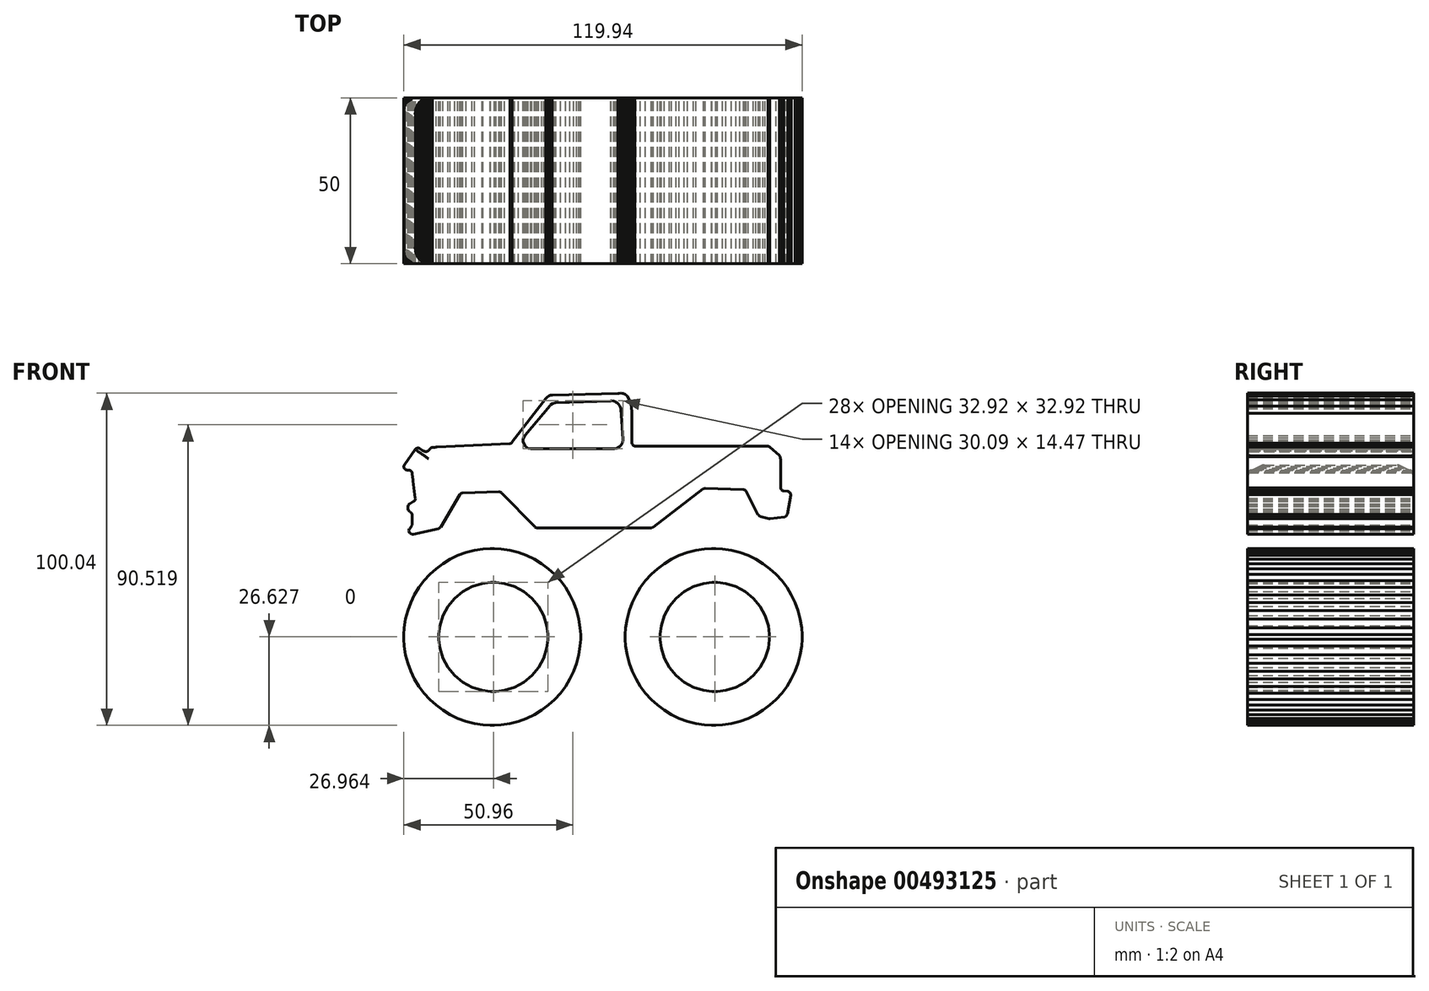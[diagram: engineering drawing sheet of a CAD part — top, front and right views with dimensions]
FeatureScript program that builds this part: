
annotation { "Feature Type Name" : "Feature", "Feature Type Description" : "" }
export const myFeature = defineFeature(function(context is Context, id is Id, definition is map)
    precondition{}
    {
        {
            var Q0;
            Q0=qCreatedBy(makeId("Front.planeOp"),FACE);
            var sketch = newSketch(context, id + "F0", { "sketchPlane" : qUnion([Q0])});
            skLineSegment(sketch, "E0", {"start": v(5.26, 34.16) * mm, "end": v(5.06, 33.96) * mm});
            skLineSegment(sketch, "E1", {"start": v(5.06, 33.96) * mm, "end": v(4.94, 33.85) * mm});
            skLineSegment(sketch, "E2", {"start": v(4.94, 33.85) * mm, "end": v(4.26, 33.45) * mm});
            skLineSegment(sketch, "E3", {"start": v(4.26, 33.45) * mm, "end": v(3.56, 33.27) * mm});
            skLineSegment(sketch, "E4", {"start": v(3.56, 33.27) * mm, "end": v(3.33, 33.27) * mm});
            skLineSegment(sketch, "E5", {"start": v(3.33, 33.27) * mm, "end": v(-21.56, 33.27) * mm});
            skLineSegment(sketch, "E6", {"start": v(-21.56, 33.27) * mm, "end": v(-21.8, 33.27) * mm});
            skLineSegment(sketch, "E7", {"start": v(-21.8, 33.27) * mm, "end": v(-22.53, 33.46) * mm});
            skLineSegment(sketch, "E8", {"start": v(-22.53, 33.46) * mm, "end": v(-23.33, 34) * mm});
            skLineSegment(sketch, "E9", {"start": v(-23.33, 34) * mm, "end": v(-23.86, 34.79) * mm});
            skLineSegment(sketch, "E10", {"start": v(-23.86, 34.79) * mm, "end": v(-24.05, 35.51) * mm});
            skLineSegment(sketch, "E11", {"start": v(-24.05, 35.51) * mm, "end": v(-24.05, 35.76) * mm});
            skLineSegment(sketch, "E12", {"start": v(-24.05, 35.76) * mm, "end": v(-24.05, 35.97) * mm});
            skLineSegment(sketch, "E13", {"start": v(-24.05, 35.97) * mm, "end": v(-23.9, 36.61) * mm});
            skLineSegment(sketch, "E14", {"start": v(-23.9, 36.61) * mm, "end": v(-23.56, 37.25) * mm});
            skLineSegment(sketch, "E15", {"start": v(-23.56, 37.25) * mm, "end": v(-23.47, 37.36) * mm});
            skLineSegment(sketch, "E16", {"start": v(-23.47, 37.36) * mm, "end": v(-15.9, 46.32) * mm});
            skLineSegment(sketch, "E17", {"start": v(-15.9, 46.32) * mm, "end": v(-15.8, 46.46) * mm});
            skLineSegment(sketch, "E18", {"start": v(-15.8, 46.46) * mm, "end": v(-15.11, 46.95) * mm});
            skLineSegment(sketch, "E19", {"start": v(-15.11, 46.95) * mm, "end": v(-14.32, 47.2) * mm});
            skLineSegment(sketch, "E20", {"start": v(-14.32, 47.2) * mm, "end": v(-14.15, 47.2) * mm});
            skLineSegment(sketch, "E21", {"start": v(-14.15, 47.2) * mm, "end": v(2.41, 47.72) * mm});
            skLineSegment(sketch, "E22", {"start": v(2.41, 47.72) * mm, "end": v(2.55, 47.73) * mm});
            skLineSegment(sketch, "E23", {"start": v(2.55, 47.73) * mm, "end": v(3.2, 47.64) * mm});
            skLineSegment(sketch, "E24", {"start": v(3.2, 47.64) * mm, "end": v(3.83, 47.38) * mm});
            skLineSegment(sketch, "E25", {"start": v(3.83, 47.38) * mm, "end": v(3.94, 47.3) * mm});
            skLineSegment(sketch, "E26", {"start": v(3.94, 47.3) * mm, "end": v(4.27, 47.1) * mm});
            skLineSegment(sketch, "E27", {"start": v(4.27, 47.1) * mm, "end": v(4.38, 47.01) * mm});
            skLineSegment(sketch, "E28", {"start": v(4.38, 47.01) * mm, "end": v(4.7, 46.72) * mm});
            skLineSegment(sketch, "E29", {"start": v(4.7, 46.72) * mm, "end": v(5.04, 46.27) * mm});
            skLineSegment(sketch, "E30", {"start": v(5.04, 46.27) * mm, "end": v(5.26, 45.75) * mm});
            skLineSegment(sketch, "E31", {"start": v(5.26, 45.75) * mm, "end": v(5.36, 45.33) * mm});
            skLineSegment(sketch, "E32", {"start": v(5.36, 45.33) * mm, "end": v(5.37, 45.2) * mm});
            skLineSegment(sketch, "E33", {"start": v(5.37, 45.2) * mm, "end": v(6.02, 36.13) * mm});
            skLineSegment(sketch, "E34", {"start": v(6.02, 36.13) * mm, "end": v(6.03, 35.94) * mm});
            skLineSegment(sketch, "E35", {"start": v(6.03, 35.94) * mm, "end": v(5.86, 35.06) * mm});
            skLineSegment(sketch, "E36", {"start": v(5.86, 35.06) * mm, "end": v(5.4, 34.29) * mm});
            skLineSegment(sketch, "E37", {"start": v(5.4, 34.29) * mm, "end": v(5.26, 34.16) * mm});
            skLineSegment(sketch, "E38", {"start": v(55.57, 20.53) * mm, "end": v(54.47, 20.57) * mm});
            skLineSegment(sketch, "E39", {"start": v(54.47, 20.57) * mm, "end": v(54.38, 20.58) * mm});
            skLineSegment(sketch, "E40", {"start": v(54.38, 20.58) * mm, "end": v(54.09, 20.67) * mm});
            skLineSegment(sketch, "E41", {"start": v(54.09, 20.67) * mm, "end": v(53.77, 20.89) * mm});
            skLineSegment(sketch, "E42", {"start": v(53.77, 20.89) * mm, "end": v(53.56, 21.21) * mm});
            skLineSegment(sketch, "E43", {"start": v(53.56, 21.21) * mm, "end": v(53.49, 21.5) * mm});
            skLineSegment(sketch, "E44", {"start": v(53.49, 21.5) * mm, "end": v(53.49, 21.6) * mm});
            skLineSegment(sketch, "E45", {"start": v(53.49, 21.6) * mm, "end": v(53.49, 30.49) * mm});
            skLineSegment(sketch, "E46", {"start": v(53.49, 30.49) * mm, "end": v(53.49, 30.6) * mm});
            skLineSegment(sketch, "E47", {"start": v(53.49, 30.6) * mm, "end": v(53.4, 30.91) * mm});
            skLineSegment(sketch, "E48", {"start": v(53.4, 30.91) * mm, "end": v(53.2, 31.21) * mm});
            skLineSegment(sketch, "E49", {"start": v(53.2, 31.21) * mm, "end": v(53.14, 31.26) * mm});
            skLineSegment(sketch, "E50", {"start": v(53.14, 31.26) * mm, "end": v(50.24, 33.82) * mm});
            skLineSegment(sketch, "E51", {"start": v(50.24, 33.82) * mm, "end": v(50.2, 33.87) * mm});
            skLineSegment(sketch, "E52", {"start": v(50.2, 33.87) * mm, "end": v(49.72, 34.08) * mm});
            skLineSegment(sketch, "E53", {"start": v(49.72, 34.08) * mm, "end": v(49.56, 34.08) * mm});
            skLineSegment(sketch, "E54", {"start": v(49.56, 34.08) * mm, "end": v(9.76, 34.08) * mm});
            skLineSegment(sketch, "E55", {"start": v(9.76, 34.08) * mm, "end": v(9.66, 34.08) * mm});
            skLineSegment(sketch, "E56", {"start": v(9.66, 34.08) * mm, "end": v(9.36, 34.16) * mm});
            skLineSegment(sketch, "E57", {"start": v(9.36, 34.16) * mm, "end": v(9.03, 34.38) * mm});
            skLineSegment(sketch, "E58", {"start": v(9.03, 34.38) * mm, "end": v(8.81, 34.71) * mm});
            skLineSegment(sketch, "E59", {"start": v(8.81, 34.71) * mm, "end": v(8.73, 35.01) * mm});
            skLineSegment(sketch, "E60", {"start": v(8.73, 35.01) * mm, "end": v(8.73, 35.11) * mm});
            skLineSegment(sketch, "E61", {"start": v(8.73, 35.11) * mm, "end": v(8.73, 43.2) * mm});
            skLineSegment(sketch, "E62", {"start": v(8.73, 43.2) * mm, "end": v(8.73, 43.93) * mm});
            skLineSegment(sketch, "E63", {"start": v(8.73, 43.93) * mm, "end": v(8.53, 46.14) * mm});
            skLineSegment(sketch, "E64", {"start": v(8.53, 46.14) * mm, "end": v(8, 48.08) * mm});
            skLineSegment(sketch, "E65", {"start": v(8, 48.08) * mm, "end": v(7.27, 49.24) * mm});
            skLineSegment(sketch, "E66", {"start": v(7.27, 49.24) * mm, "end": v(6.68, 49.73) * mm});
            skLineSegment(sketch, "E67", {"start": v(6.68, 49.73) * mm, "end": v(6.46, 49.84) * mm});
            skLineSegment(sketch, "E68", {"start": v(6.46, 49.84) * mm, "end": v(6.34, 49.9) * mm});
            skLineSegment(sketch, "E69", {"start": v(6.34, 49.9) * mm, "end": v(5.94, 49.98) * mm});
            skLineSegment(sketch, "E70", {"start": v(5.94, 49.98) * mm, "end": v(5.35, 50.02) * mm});
            skLineSegment(sketch, "E71", {"start": v(5.35, 50.02) * mm, "end": v(4.83, 50) * mm});
            skLineSegment(sketch, "E72", {"start": v(4.83, 50) * mm, "end": v(4.57, 50) * mm});
            skLineSegment(sketch, "E73", {"start": v(4.57, 50) * mm, "end": v(4.52, 50) * mm});
            skLineSegment(sketch, "E74", {"start": v(4.52, 50) * mm, "end": v(-15.2, 49.48) * mm});
            skLineSegment(sketch, "E75", {"start": v(-15.2, 49.48) * mm, "end": v(-15.35, 49.48) * mm});
            skLineSegment(sketch, "E76", {"start": v(-15.35, 49.48) * mm, "end": v(-15.79, 49.4) * mm});
            skLineSegment(sketch, "E77", {"start": v(-15.79, 49.4) * mm, "end": v(-16.33, 49.19) * mm});
            skLineSegment(sketch, "E78", {"start": v(-16.33, 49.19) * mm, "end": v(-16.81, 48.85) * mm});
            skLineSegment(sketch, "E79", {"start": v(-16.81, 48.85) * mm, "end": v(-17.12, 48.53) * mm});
            skLineSegment(sketch, "E80", {"start": v(-17.12, 48.53) * mm, "end": v(-17.2, 48.41) * mm});
            skLineSegment(sketch, "E81", {"start": v(-17.2, 48.41) * mm, "end": v(-27.3, 35.31) * mm});
            skLineSegment(sketch, "E82", {"start": v(-27.3, 35.31) * mm, "end": v(-27.35, 35.25) * mm});
            skLineSegment(sketch, "E83", {"start": v(-27.35, 35.25) * mm, "end": v(-27.65, 35) * mm});
            skLineSegment(sketch, "E84", {"start": v(-27.65, 35) * mm, "end": v(-28.02, 34.88) * mm});
            skLineSegment(sketch, "E85", {"start": v(-28.02, 34.88) * mm, "end": v(-28.1, 34.87) * mm});
            skLineSegment(sketch, "E86", {"start": v(-28.1, 34.87) * mm, "end": v(-51.32, 33.71) * mm});
            skLineSegment(sketch, "E87", {"start": v(-51.32, 33.71) * mm, "end": v(-51.42, 33.7) * mm});
            skLineSegment(sketch, "E88", {"start": v(-51.42, 33.7) * mm, "end": v(-51.85, 33.54) * mm});
            skLineSegment(sketch, "E89", {"start": v(-51.85, 33.54) * mm, "end": v(-52.17, 33.22) * mm});
            skLineSegment(sketch, "E90", {"start": v(-52.17, 33.22) * mm, "end": v(-52.2, 33.13) * mm});
            skLineSegment(sketch, "E91", {"start": v(-52.2, 33.13) * mm, "end": v(-52.24, 33.06) * mm});
            skLineSegment(sketch, "E92", {"start": v(-52.24, 33.06) * mm, "end": v(-52.36, 32.88) * mm});
            skLineSegment(sketch, "E93", {"start": v(-52.36, 32.88) * mm, "end": v(-52.6, 32.65) * mm});
            skLineSegment(sketch, "E94", {"start": v(-52.6, 32.65) * mm, "end": v(-52.96, 32.5) * mm});
            skLineSegment(sketch, "E95", {"start": v(-52.96, 32.5) * mm, "end": v(-53.32, 32.44) * mm});
            skLineSegment(sketch, "E96", {"start": v(-53.32, 32.44) * mm, "end": v(-53.44, 32.45) * mm});
            skLineSegment(sketch, "E97", {"start": v(-53.44, 32.45) * mm, "end": v(-53.59, 32.46) * mm});
            skLineSegment(sketch, "E98", {"start": v(-53.59, 32.46) * mm, "end": v(-54.28, 32.7) * mm});
            skLineSegment(sketch, "E99", {"start": v(-54.28, 32.7) * mm, "end": v(-54.87, 33.13) * mm});
            skLineSegment(sketch, "E100", {"start": v(-54.87, 33.13) * mm, "end": v(-54.97, 33.23) * mm});
            skLineSegment(sketch, "E101", {"start": v(-54.97, 33.23) * mm, "end": v(-55.05, 33.3) * mm});
            skLineSegment(sketch, "E102", {"start": v(-55.05, 33.3) * mm, "end": v(-55.36, 33.47) * mm});
            skLineSegment(sketch, "E103", {"start": v(-55.36, 33.47) * mm, "end": v(-55.79, 33.53) * mm});
            skLineSegment(sketch, "E104", {"start": v(-55.79, 33.53) * mm, "end": v(-56.2, 33.4) * mm});
            skLineSegment(sketch, "E105", {"start": v(-56.2, 33.4) * mm, "end": v(-56.48, 33.19) * mm});
            skLineSegment(sketch, "E106", {"start": v(-56.48, 33.19) * mm, "end": v(-56.54, 33.1) * mm});
            skLineSegment(sketch, "E107", {"start": v(-56.54, 33.1) * mm, "end": v(-59.78, 28.5) * mm});
            skLineSegment(sketch, "E108", {"start": v(-59.78, 28.5) * mm, "end": v(-59.86, 28.38) * mm});
            skLineSegment(sketch, "E109", {"start": v(-59.86, 28.38) * mm, "end": v(-59.97, 27.96) * mm});
            skLineSegment(sketch, "E110", {"start": v(-59.97, 27.96) * mm, "end": v(-59.85, 27.43) * mm});
            skLineSegment(sketch, "E111", {"start": v(-59.85, 27.43) * mm, "end": v(-59.49, 27.03) * mm});
            skLineSegment(sketch, "E112", {"start": v(-59.49, 27.03) * mm, "end": v(-59.07, 26.87) * mm});
            skLineSegment(sketch, "E113", {"start": v(-59.07, 26.87) * mm, "end": v(-58.93, 26.87) * mm});
            skLineSegment(sketch, "E114", {"start": v(-58.93, 26.87) * mm, "end": v(-58.5, 26.87) * mm});
            skLineSegment(sketch, "E115", {"start": v(-58.5, 26.87) * mm, "end": v(-58.4, 26.87) * mm});
            skLineSegment(sketch, "E116", {"start": v(-58.4, 26.87) * mm, "end": v(-58.13, 26.8) * mm});
            skLineSegment(sketch, "E117", {"start": v(-58.13, 26.8) * mm, "end": v(-57.81, 26.62) * mm});
            skLineSegment(sketch, "E118", {"start": v(-57.81, 26.62) * mm, "end": v(-57.59, 26.33) * mm});
            skLineSegment(sketch, "E119", {"start": v(-57.59, 26.33) * mm, "end": v(-57.48, 26.06) * mm});
            skLineSegment(sketch, "E120", {"start": v(-57.48, 26.06) * mm, "end": v(-57.47, 25.97) * mm});
            skLineSegment(sketch, "E121", {"start": v(-57.47, 25.97) * mm, "end": v(-56.52, 18.43) * mm});
            skLineSegment(sketch, "E122", {"start": v(-56.52, 18.43) * mm, "end": v(-56.5, 18.33) * mm});
            skLineSegment(sketch, "E123", {"start": v(-56.5, 18.33) * mm, "end": v(-56.61, 17.85) * mm});
            skLineSegment(sketch, "E124", {"start": v(-56.61, 17.85) * mm, "end": v(-56.93, 17.47) * mm});
            skLineSegment(sketch, "E125", {"start": v(-56.93, 17.47) * mm, "end": v(-57.02, 17.41) * mm});
            skLineSegment(sketch, "E126", {"start": v(-57.02, 17.41) * mm, "end": v(-58.24, 16.7) * mm});
            skLineSegment(sketch, "E127", {"start": v(-58.24, 16.7) * mm, "end": v(-58.32, 16.65) * mm});
            skLineSegment(sketch, "E128", {"start": v(-58.32, 16.65) * mm, "end": v(-58.6, 16.32) * mm});
            skLineSegment(sketch, "E129", {"start": v(-58.6, 16.32) * mm, "end": v(-58.74, 15.94) * mm});
            skLineSegment(sketch, "E130", {"start": v(-58.74, 15.94) * mm, "end": v(-58.74, 15.8) * mm});
            skLineSegment(sketch, "E131", {"start": v(-58.74, 15.8) * mm, "end": v(-58.74, 15.3) * mm});
            skLineSegment(sketch, "E132", {"start": v(-58.74, 15.3) * mm, "end": v(-58.74, 15.16) * mm});
            skLineSegment(sketch, "E133", {"start": v(-58.74, 15.16) * mm, "end": v(-58.58, 14.74) * mm});
            skLineSegment(sketch, "E134", {"start": v(-58.58, 14.74) * mm, "end": v(-58.23, 14.4) * mm});
            skLineSegment(sketch, "E135", {"start": v(-58.23, 14.4) * mm, "end": v(-58.13, 14.36) * mm});
            skLineSegment(sketch, "E136", {"start": v(-58.13, 14.36) * mm, "end": v(-58.04, 14.32) * mm});
            skLineSegment(sketch, "E137", {"start": v(-58.04, 14.32) * mm, "end": v(-57.69, 13.98) * mm});
            skLineSegment(sketch, "E138", {"start": v(-57.69, 13.98) * mm, "end": v(-57.52, 13.55) * mm});
            skLineSegment(sketch, "E139", {"start": v(-57.52, 13.55) * mm, "end": v(-57.52, 13.41) * mm});
            skLineSegment(sketch, "E140", {"start": v(-57.52, 13.41) * mm, "end": v(-57.52, 10.48) * mm});
            skLineSegment(sketch, "E141", {"start": v(-57.52, 10.48) * mm, "end": v(-57.52, 10.33) * mm});
            skLineSegment(sketch, "E142", {"start": v(-57.52, 10.33) * mm, "end": v(-57.7, 9.9) * mm});
            skLineSegment(sketch, "E143", {"start": v(-57.7, 9.9) * mm, "end": v(-57.73, 9.86) * mm});
            skLineSegment(sketch, "E144", {"start": v(-57.73, 9.86) * mm, "end": v(-58.2, 9.22) * mm});
            skLineSegment(sketch, "E145", {"start": v(-58.2, 9.22) * mm, "end": v(-58.29, 9.12) * mm});
            skLineSegment(sketch, "E146", {"start": v(-58.29, 9.12) * mm, "end": v(-58.41, 8.53) * mm});
            skLineSegment(sketch, "E147", {"start": v(-58.41, 8.53) * mm, "end": v(-58.2, 7.97) * mm});
            skLineSegment(sketch, "E148", {"start": v(-58.2, 7.97) * mm, "end": v(-58.11, 7.87) * mm});
            skLineSegment(sketch, "E149", {"start": v(-58.11, 7.87) * mm, "end": v(-58.06, 7.82) * mm});
            skLineSegment(sketch, "E150", {"start": v(-58.06, 7.82) * mm, "end": v(-58, 7.76) * mm});
            skLineSegment(sketch, "E151", {"start": v(-58, 7.76) * mm, "end": v(-57.62, 7.56) * mm});
            skLineSegment(sketch, "E152", {"start": v(-57.62, 7.56) * mm, "end": v(-57.19, 7.52) * mm});
            skLineSegment(sketch, "E153", {"start": v(-57.19, 7.52) * mm, "end": v(-57.1, 7.54) * mm});
            skLineSegment(sketch, "E154", {"start": v(-57.1, 7.54) * mm, "end": v(-49.52, 9.23) * mm});
            skLineSegment(sketch, "E155", {"start": v(-49.52, 9.23) * mm, "end": v(-49.45, 9.24) * mm});
            skLineSegment(sketch, "E156", {"start": v(-49.45, 9.24) * mm, "end": v(-49.14, 9.4) * mm});
            skLineSegment(sketch, "E157", {"start": v(-49.14, 9.4) * mm, "end": v(-48.9, 9.65) * mm});
            skLineSegment(sketch, "E158", {"start": v(-48.9, 9.65) * mm, "end": v(-48.86, 9.7) * mm});
            skLineSegment(sketch, "E159", {"start": v(-48.86, 9.7) * mm, "end": v(-43.11, 19.45) * mm});
            skLineSegment(sketch, "E160", {"start": v(-43.11, 19.45) * mm, "end": v(-43.07, 19.52) * mm});
            skLineSegment(sketch, "E161", {"start": v(-43.07, 19.52) * mm, "end": v(-42.75, 19.81) * mm});
            skLineSegment(sketch, "E162", {"start": v(-42.75, 19.81) * mm, "end": v(-42.35, 19.95) * mm});
            skLineSegment(sketch, "E163", {"start": v(-42.35, 19.95) * mm, "end": v(-42.26, 19.95) * mm});
            skLineSegment(sketch, "E164", {"start": v(-42.26, 19.95) * mm, "end": v(-31.31, 20.33) * mm});
            skLineSegment(sketch, "E165", {"start": v(-31.31, 20.33) * mm, "end": v(-31.24, 20.33) * mm});
            skLineSegment(sketch, "E166", {"start": v(-31.24, 20.33) * mm, "end": v(-30.9, 20.25) * mm});
            skLineSegment(sketch, "E167", {"start": v(-30.9, 20.25) * mm, "end": v(-30.59, 20.07) * mm});
            skLineSegment(sketch, "E168", {"start": v(-30.59, 20.07) * mm, "end": v(-30.54, 20.02) * mm});
            skLineSegment(sketch, "E169", {"start": v(-30.54, 20.02) * mm, "end": v(-20.55, 9.77) * mm});
            skLineSegment(sketch, "E170", {"start": v(-20.55, 9.77) * mm, "end": v(-20.5, 9.72) * mm});
            skLineSegment(sketch, "E171", {"start": v(-20.5, 9.72) * mm, "end": v(-20.21, 9.54) * mm});
            skLineSegment(sketch, "E172", {"start": v(-20.21, 9.54) * mm, "end": v(-19.91, 9.46) * mm});
            skLineSegment(sketch, "E173", {"start": v(-19.91, 9.46) * mm, "end": v(-19.81, 9.46) * mm});
            skLineSegment(sketch, "E174", {"start": v(-19.81, 9.46) * mm, "end": v(14.5, 9.46) * mm});
            skLineSegment(sketch, "E175", {"start": v(14.5, 9.46) * mm, "end": v(14.66, 9.46) * mm});
            skLineSegment(sketch, "E176", {"start": v(14.66, 9.46) * mm, "end": v(15.08, 9.64) * mm});
            skLineSegment(sketch, "E177", {"start": v(15.08, 9.64) * mm, "end": v(15.13, 9.67) * mm});
            skLineSegment(sketch, "E178", {"start": v(15.13, 9.67) * mm, "end": v(30.2, 21.2) * mm});
            skLineSegment(sketch, "E179", {"start": v(30.2, 21.2) * mm, "end": v(30.25, 21.24) * mm});
            skLineSegment(sketch, "E180", {"start": v(30.25, 21.24) * mm, "end": v(30.8, 21.42) * mm});
            skLineSegment(sketch, "E181", {"start": v(30.8, 21.42) * mm, "end": v(30.86, 21.42) * mm});
            skLineSegment(sketch, "E182", {"start": v(30.86, 21.42) * mm, "end": v(42.27, 21.04) * mm});
            skLineSegment(sketch, "E183", {"start": v(42.27, 21.04) * mm, "end": v(42.36, 21.04) * mm});
            skLineSegment(sketch, "E184", {"start": v(42.36, 21.04) * mm, "end": v(42.79, 20.88) * mm});
            skLineSegment(sketch, "E185", {"start": v(42.79, 20.88) * mm, "end": v(43.1, 20.56) * mm});
            skLineSegment(sketch, "E186", {"start": v(43.1, 20.56) * mm, "end": v(43.15, 20.48) * mm});
            skLineSegment(sketch, "E187", {"start": v(43.15, 20.48) * mm, "end": v(46.74, 13.42) * mm});
            skLineSegment(sketch, "E188", {"start": v(46.74, 13.42) * mm, "end": v(46.78, 13.35) * mm});
            skLineSegment(sketch, "E189", {"start": v(46.78, 13.35) * mm, "end": v(47.02, 13.08) * mm});
            skLineSegment(sketch, "E190", {"start": v(47.02, 13.08) * mm, "end": v(47.34, 12.9) * mm});
            skLineSegment(sketch, "E191", {"start": v(47.34, 12.9) * mm, "end": v(47.41, 12.88) * mm});
            skLineSegment(sketch, "E192", {"start": v(47.41, 12.88) * mm, "end": v(50.03, 12.23) * mm});
            skLineSegment(sketch, "E193", {"start": v(50.03, 12.23) * mm, "end": v(50.06, 12.22) * mm});
            skLineSegment(sketch, "E194", {"start": v(50.06, 12.22) * mm, "end": v(50.38, 12.2) * mm});
            skLineSegment(sketch, "E195", {"start": v(50.38, 12.2) * mm, "end": v(50.42, 12.2) * mm});
            skLineSegment(sketch, "E196", {"start": v(50.42, 12.2) * mm, "end": v(54.64, 12.76) * mm});
            skLineSegment(sketch, "E197", {"start": v(54.64, 12.76) * mm, "end": v(54.75, 12.78) * mm});
            skLineSegment(sketch, "E198", {"start": v(54.75, 12.78) * mm, "end": v(55.22, 13.04) * mm});
            skLineSegment(sketch, "E199", {"start": v(55.22, 13.04) * mm, "end": v(55.5, 13.5) * mm});
            skLineSegment(sketch, "E200", {"start": v(55.5, 13.5) * mm, "end": v(55.52, 13.6) * mm});
            skLineSegment(sketch, "E201", {"start": v(55.52, 13.6) * mm, "end": v(56.54, 19.32) * mm});
            skLineSegment(sketch, "E202", {"start": v(56.54, 19.32) * mm, "end": v(56.56, 19.42) * mm});
            skLineSegment(sketch, "E203", {"start": v(56.56, 19.42) * mm, "end": v(56.52, 19.76) * mm});
            skLineSegment(sketch, "E204", {"start": v(56.52, 19.76) * mm, "end": v(56.33, 20.14) * mm});
            skLineSegment(sketch, "E205", {"start": v(56.33, 20.14) * mm, "end": v(56, 20.41) * mm});
            skLineSegment(sketch, "E206", {"start": v(56, 20.41) * mm, "end": v(55.68, 20.52) * mm});
            skLineSegment(sketch, "E207", {"start": v(55.68, 20.52) * mm, "end": v(55.57, 20.53) * mm});
            skLineSegment(sketch, "E208", {"start": v(-6.71, -23.4) * mm, "end": v(-6.71, -24.07) * mm});
            skLineSegment(sketch, "E209", {"start": v(-6.71, -24.07) * mm, "end": v(-6.85, -26.12) * mm});
            skLineSegment(sketch, "E210", {"start": v(-6.85, -26.12) * mm, "end": v(-7.25, -28.76) * mm});
            skLineSegment(sketch, "E211", {"start": v(-7.25, -28.76) * mm, "end": v(-7.9, -31.31) * mm});
            skLineSegment(sketch, "E212", {"start": v(-7.9, -31.31) * mm, "end": v(-8.8, -33.76) * mm});
            skLineSegment(sketch, "E213", {"start": v(-8.8, -33.76) * mm, "end": v(-9.93, -36.08) * mm});
            skLineSegment(sketch, "E214", {"start": v(-9.93, -36.08) * mm, "end": v(-11.26, -38.28) * mm});
            skLineSegment(sketch, "E215", {"start": v(-11.26, -38.28) * mm, "end": v(-12.8, -40.33) * mm});
            skLineSegment(sketch, "E216", {"start": v(-12.8, -40.33) * mm, "end": v(-14.51, -42.22) * mm});
            skLineSegment(sketch, "E217", {"start": v(-14.51, -42.22) * mm, "end": v(-16.4, -43.94) * mm});
            skLineSegment(sketch, "E218", {"start": v(-16.4, -43.94) * mm, "end": v(-18.45, -45.47) * mm});
            skLineSegment(sketch, "E219", {"start": v(-18.45, -45.47) * mm, "end": v(-20.65, -46.8) * mm});
            skLineSegment(sketch, "E220", {"start": v(-20.65, -46.8) * mm, "end": v(-22.97, -47.93) * mm});
            skLineSegment(sketch, "E221", {"start": v(-22.97, -47.93) * mm, "end": v(-25.42, -48.82) * mm});
            skLineSegment(sketch, "E222", {"start": v(-25.42, -48.82) * mm, "end": v(-27.97, -49.48) * mm});
            skLineSegment(sketch, "E223", {"start": v(-27.97, -49.48) * mm, "end": v(-30.62, -49.88) * mm});
            skLineSegment(sketch, "E224", {"start": v(-30.62, -49.88) * mm, "end": v(-32.66, -50.02) * mm});
            skLineSegment(sketch, "E225", {"start": v(-32.66, -50.02) * mm, "end": v(-33.34, -50.02) * mm});
            skLineSegment(sketch, "E226", {"start": v(-33.34, -50.02) * mm, "end": v(-34.02, -50.02) * mm});
            skLineSegment(sketch, "E227", {"start": v(-34.02, -50.02) * mm, "end": v(-36.06, -49.88) * mm});
            skLineSegment(sketch, "E228", {"start": v(-36.06, -49.88) * mm, "end": v(-38.7, -49.48) * mm});
            skLineSegment(sketch, "E229", {"start": v(-38.7, -49.48) * mm, "end": v(-41.26, -48.82) * mm});
            skLineSegment(sketch, "E230", {"start": v(-41.26, -48.82) * mm, "end": v(-43.7, -47.93) * mm});
            skLineSegment(sketch, "E231", {"start": v(-43.7, -47.93) * mm, "end": v(-46.03, -46.8) * mm});
            skLineSegment(sketch, "E232", {"start": v(-46.03, -46.8) * mm, "end": v(-48.23, -45.47) * mm});
            skLineSegment(sketch, "E233", {"start": v(-48.23, -45.47) * mm, "end": v(-50.28, -43.94) * mm});
            skLineSegment(sketch, "E234", {"start": v(-50.28, -43.94) * mm, "end": v(-52.17, -42.22) * mm});
            skLineSegment(sketch, "E235", {"start": v(-52.17, -42.22) * mm, "end": v(-53.89, -40.33) * mm});
            skLineSegment(sketch, "E236", {"start": v(-53.89, -40.33) * mm, "end": v(-55.42, -38.28) * mm});
            skLineSegment(sketch, "E237", {"start": v(-55.42, -38.28) * mm, "end": v(-56.75, -36.08) * mm});
            skLineSegment(sketch, "E238", {"start": v(-56.75, -36.08) * mm, "end": v(-57.88, -33.76) * mm});
            skLineSegment(sketch, "E239", {"start": v(-57.88, -33.76) * mm, "end": v(-58.77, -31.31) * mm});
            skLineSegment(sketch, "E240", {"start": v(-58.77, -31.31) * mm, "end": v(-59.43, -28.76) * mm});
            skLineSegment(sketch, "E241", {"start": v(-59.43, -28.76) * mm, "end": v(-59.83, -26.12) * mm});
            skLineSegment(sketch, "E242", {"start": v(-59.83, -26.12) * mm, "end": v(-59.97, -24.07) * mm});
            skLineSegment(sketch, "E243", {"start": v(-59.97, -24.07) * mm, "end": v(-59.97, -23.4) * mm});
            skLineSegment(sketch, "E244", {"start": v(-59.97, -23.4) * mm, "end": v(-59.97, -22.71) * mm});
            skLineSegment(sketch, "E245", {"start": v(-59.97, -22.71) * mm, "end": v(-59.83, -20.67) * mm});
            skLineSegment(sketch, "E246", {"start": v(-59.83, -20.67) * mm, "end": v(-59.43, -18.03) * mm});
            skLineSegment(sketch, "E247", {"start": v(-59.43, -18.03) * mm, "end": v(-58.77, -15.47) * mm});
            skLineSegment(sketch, "E248", {"start": v(-58.77, -15.47) * mm, "end": v(-57.88, -13.03) * mm});
            skLineSegment(sketch, "E249", {"start": v(-57.88, -13.03) * mm, "end": v(-56.75, -10.7) * mm});
            skLineSegment(sketch, "E250", {"start": v(-56.75, -10.7) * mm, "end": v(-55.42, -8.5) * mm});
            skLineSegment(sketch, "E251", {"start": v(-55.42, -8.5) * mm, "end": v(-53.89, -6.45) * mm});
            skLineSegment(sketch, "E252", {"start": v(-53.89, -6.45) * mm, "end": v(-52.17, -4.56) * mm});
            skLineSegment(sketch, "E253", {"start": v(-52.17, -4.56) * mm, "end": v(-50.28, -2.85) * mm});
            skLineSegment(sketch, "E254", {"start": v(-50.28, -2.85) * mm, "end": v(-48.23, -1.31) * mm});
            skLineSegment(sketch, "E255", {"start": v(-48.23, -1.31) * mm, "end": v(-46.03, 0.02) * mm});
            skLineSegment(sketch, "E256", {"start": v(-46.03, 0.02) * mm, "end": v(-43.7, 1.14) * mm});
            skLineSegment(sketch, "E257", {"start": v(-43.7, 1.14) * mm, "end": v(-41.26, 2.04) * mm});
            skLineSegment(sketch, "E258", {"start": v(-41.26, 2.04) * mm, "end": v(-38.7, 2.7) * mm});
            skLineSegment(sketch, "E259", {"start": v(-38.7, 2.7) * mm, "end": v(-36.06, 3.1) * mm});
            skLineSegment(sketch, "E260", {"start": v(-36.06, 3.1) * mm, "end": v(-34.02, 3.23) * mm});
            skLineSegment(sketch, "E261", {"start": v(-34.02, 3.23) * mm, "end": v(-33.34, 3.23) * mm});
            skLineSegment(sketch, "E262", {"start": v(-33.34, 3.23) * mm, "end": v(-32.66, 3.23) * mm});
            skLineSegment(sketch, "E263", {"start": v(-32.66, 3.23) * mm, "end": v(-30.62, 3.1) * mm});
            skLineSegment(sketch, "E264", {"start": v(-30.62, 3.1) * mm, "end": v(-27.97, 2.7) * mm});
            skLineSegment(sketch, "E265", {"start": v(-27.97, 2.7) * mm, "end": v(-25.42, 2.04) * mm});
            skLineSegment(sketch, "E266", {"start": v(-25.42, 2.04) * mm, "end": v(-22.97, 1.14) * mm});
            skLineSegment(sketch, "E267", {"start": v(-22.97, 1.14) * mm, "end": v(-20.65, 0.02) * mm});
            skLineSegment(sketch, "E268", {"start": v(-20.65, 0.02) * mm, "end": v(-18.45, -1.31) * mm});
            skLineSegment(sketch, "E269", {"start": v(-18.45, -1.31) * mm, "end": v(-16.4, -2.85) * mm});
            skLineSegment(sketch, "E270", {"start": v(-16.4, -2.85) * mm, "end": v(-14.51, -4.56) * mm});
            skLineSegment(sketch, "E271", {"start": v(-14.51, -4.56) * mm, "end": v(-12.8, -6.45) * mm});
            skLineSegment(sketch, "E272", {"start": v(-12.8, -6.45) * mm, "end": v(-11.26, -8.5) * mm});
            skLineSegment(sketch, "E273", {"start": v(-11.26, -8.5) * mm, "end": v(-9.93, -10.7) * mm});
            skLineSegment(sketch, "E274", {"start": v(-9.93, -10.7) * mm, "end": v(-8.8, -13.03) * mm});
            skLineSegment(sketch, "E275", {"start": v(-8.8, -13.03) * mm, "end": v(-7.9, -15.47) * mm});
            skLineSegment(sketch, "E276", {"start": v(-7.9, -15.47) * mm, "end": v(-7.25, -18.03) * mm});
            skLineSegment(sketch, "E277", {"start": v(-7.25, -18.03) * mm, "end": v(-6.85, -20.67) * mm});
            skLineSegment(sketch, "E278", {"start": v(-6.85, -20.67) * mm, "end": v(-6.71, -22.71) * mm});
            skLineSegment(sketch, "E279", {"start": v(-6.71, -22.71) * mm, "end": v(-6.71, -23.4) * mm});
            skLineSegment(sketch, "E280", {"start": v(59.97, -23.4) * mm, "end": v(59.97, -24.07) * mm});
            skLineSegment(sketch, "E281", {"start": v(59.97, -24.07) * mm, "end": v(59.83, -26.12) * mm});
            skLineSegment(sketch, "E282", {"start": v(59.83, -26.12) * mm, "end": v(59.43, -28.76) * mm});
            skLineSegment(sketch, "E283", {"start": v(59.43, -28.76) * mm, "end": v(58.77, -31.31) * mm});
            skLineSegment(sketch, "E284", {"start": v(58.77, -31.31) * mm, "end": v(57.87, -33.76) * mm});
            skLineSegment(sketch, "E285", {"start": v(57.87, -33.76) * mm, "end": v(56.75, -36.08) * mm});
            skLineSegment(sketch, "E286", {"start": v(56.75, -36.08) * mm, "end": v(55.42, -38.28) * mm});
            skLineSegment(sketch, "E287", {"start": v(55.42, -38.28) * mm, "end": v(53.89, -40.33) * mm});
            skLineSegment(sketch, "E288", {"start": v(53.89, -40.33) * mm, "end": v(52.17, -42.22) * mm});
            skLineSegment(sketch, "E289", {"start": v(52.17, -42.22) * mm, "end": v(50.28, -43.94) * mm});
            skLineSegment(sketch, "E290", {"start": v(50.28, -43.94) * mm, "end": v(48.23, -45.47) * mm});
            skLineSegment(sketch, "E291", {"start": v(48.23, -45.47) * mm, "end": v(46.03, -46.8) * mm});
            skLineSegment(sketch, "E292", {"start": v(46.03, -46.8) * mm, "end": v(43.7, -47.93) * mm});
            skLineSegment(sketch, "E293", {"start": v(43.7, -47.93) * mm, "end": v(41.26, -48.82) * mm});
            skLineSegment(sketch, "E294", {"start": v(41.26, -48.82) * mm, "end": v(38.7, -49.48) * mm});
            skLineSegment(sketch, "E295", {"start": v(38.7, -49.48) * mm, "end": v(36.06, -49.88) * mm});
            skLineSegment(sketch, "E296", {"start": v(36.06, -49.88) * mm, "end": v(34.02, -50.02) * mm});
            skLineSegment(sketch, "E297", {"start": v(34.02, -50.02) * mm, "end": v(33.34, -50.02) * mm});
            skLineSegment(sketch, "E298", {"start": v(33.34, -50.02) * mm, "end": v(32.66, -50.02) * mm});
            skLineSegment(sketch, "E299", {"start": v(32.66, -50.02) * mm, "end": v(30.62, -49.88) * mm});
            skLineSegment(sketch, "E300", {"start": v(30.62, -49.88) * mm, "end": v(27.97, -49.48) * mm});
            skLineSegment(sketch, "E301", {"start": v(27.97, -49.48) * mm, "end": v(25.42, -48.82) * mm});
            skLineSegment(sketch, "E302", {"start": v(25.42, -48.82) * mm, "end": v(22.97, -47.93) * mm});
            skLineSegment(sketch, "E303", {"start": v(22.97, -47.93) * mm, "end": v(20.65, -46.8) * mm});
            skLineSegment(sketch, "E304", {"start": v(20.65, -46.8) * mm, "end": v(18.45, -45.47) * mm});
            skLineSegment(sketch, "E305", {"start": v(18.45, -45.47) * mm, "end": v(16.4, -43.94) * mm});
            skLineSegment(sketch, "E306", {"start": v(16.4, -43.94) * mm, "end": v(14.51, -42.22) * mm});
            skLineSegment(sketch, "E307", {"start": v(14.51, -42.22) * mm, "end": v(12.8, -40.33) * mm});
            skLineSegment(sketch, "E308", {"start": v(12.8, -40.33) * mm, "end": v(11.26, -38.28) * mm});
            skLineSegment(sketch, "E309", {"start": v(11.26, -38.28) * mm, "end": v(9.93, -36.08) * mm});
            skLineSegment(sketch, "E310", {"start": v(9.93, -36.08) * mm, "end": v(8.8, -33.76) * mm});
            skLineSegment(sketch, "E311", {"start": v(8.8, -33.76) * mm, "end": v(7.9, -31.31) * mm});
            skLineSegment(sketch, "E312", {"start": v(7.9, -31.31) * mm, "end": v(7.25, -28.76) * mm});
            skLineSegment(sketch, "E313", {"start": v(7.25, -28.76) * mm, "end": v(6.85, -26.12) * mm});
            skLineSegment(sketch, "E314", {"start": v(6.85, -26.12) * mm, "end": v(6.71, -24.07) * mm});
            skLineSegment(sketch, "E315", {"start": v(6.71, -24.07) * mm, "end": v(6.71, -23.4) * mm});
            skLineSegment(sketch, "E316", {"start": v(6.71, -23.4) * mm, "end": v(6.71, -22.71) * mm});
            skLineSegment(sketch, "E317", {"start": v(6.71, -22.71) * mm, "end": v(6.85, -20.67) * mm});
            skLineSegment(sketch, "E318", {"start": v(6.85, -20.67) * mm, "end": v(7.25, -18.03) * mm});
            skLineSegment(sketch, "E319", {"start": v(7.25, -18.03) * mm, "end": v(7.9, -15.47) * mm});
            skLineSegment(sketch, "E320", {"start": v(7.9, -15.47) * mm, "end": v(8.8, -13.03) * mm});
            skLineSegment(sketch, "E321", {"start": v(8.8, -13.03) * mm, "end": v(9.93, -10.7) * mm});
            skLineSegment(sketch, "E322", {"start": v(9.93, -10.7) * mm, "end": v(11.26, -8.5) * mm});
            skLineSegment(sketch, "E323", {"start": v(11.26, -8.5) * mm, "end": v(12.8, -6.45) * mm});
            skLineSegment(sketch, "E324", {"start": v(12.8, -6.45) * mm, "end": v(14.51, -4.56) * mm});
            skLineSegment(sketch, "E325", {"start": v(14.51, -4.56) * mm, "end": v(16.4, -2.85) * mm});
            skLineSegment(sketch, "E326", {"start": v(16.4, -2.85) * mm, "end": v(18.45, -1.31) * mm});
            skLineSegment(sketch, "E327", {"start": v(18.45, -1.31) * mm, "end": v(20.65, 0.02) * mm});
            skLineSegment(sketch, "E328", {"start": v(20.65, 0.02) * mm, "end": v(22.97, 1.14) * mm});
            skLineSegment(sketch, "E329", {"start": v(22.97, 1.14) * mm, "end": v(25.42, 2.04) * mm});
            skLineSegment(sketch, "E330", {"start": v(25.42, 2.04) * mm, "end": v(27.97, 2.7) * mm});
            skLineSegment(sketch, "E331", {"start": v(27.97, 2.7) * mm, "end": v(30.62, 3.1) * mm});
            skLineSegment(sketch, "E332", {"start": v(30.62, 3.1) * mm, "end": v(32.66, 3.23) * mm});
            skLineSegment(sketch, "E333", {"start": v(32.66, 3.23) * mm, "end": v(33.34, 3.23) * mm});
            skLineSegment(sketch, "E334", {"start": v(33.34, 3.23) * mm, "end": v(34.02, 3.23) * mm});
            skLineSegment(sketch, "E335", {"start": v(34.02, 3.23) * mm, "end": v(36.06, 3.1) * mm});
            skLineSegment(sketch, "E336", {"start": v(36.06, 3.1) * mm, "end": v(38.7, 2.7) * mm});
            skLineSegment(sketch, "E337", {"start": v(38.7, 2.7) * mm, "end": v(41.26, 2.04) * mm});
            skLineSegment(sketch, "E338", {"start": v(41.26, 2.04) * mm, "end": v(43.7, 1.14) * mm});
            skLineSegment(sketch, "E339", {"start": v(43.7, 1.14) * mm, "end": v(46.03, 0.02) * mm});
            skLineSegment(sketch, "E340", {"start": v(46.03, 0.02) * mm, "end": v(48.23, -1.31) * mm});
            skLineSegment(sketch, "E341", {"start": v(48.23, -1.31) * mm, "end": v(50.28, -2.85) * mm});
            skLineSegment(sketch, "E342", {"start": v(50.28, -2.85) * mm, "end": v(52.17, -4.56) * mm});
            skLineSegment(sketch, "E343", {"start": v(52.17, -4.56) * mm, "end": v(53.89, -6.45) * mm});
            skLineSegment(sketch, "E344", {"start": v(53.89, -6.45) * mm, "end": v(55.42, -8.5) * mm});
            skLineSegment(sketch, "E345", {"start": v(55.42, -8.5) * mm, "end": v(56.75, -10.7) * mm});
            skLineSegment(sketch, "E346", {"start": v(56.75, -10.7) * mm, "end": v(57.87, -13.03) * mm});
            skLineSegment(sketch, "E347", {"start": v(57.87, -13.03) * mm, "end": v(58.77, -15.47) * mm});
            skLineSegment(sketch, "E348", {"start": v(58.77, -15.47) * mm, "end": v(59.43, -18.03) * mm});
            skLineSegment(sketch, "E349", {"start": v(59.43, -18.03) * mm, "end": v(59.83, -20.67) * mm});
            skLineSegment(sketch, "E350", {"start": v(59.83, -20.67) * mm, "end": v(59.97, -22.71) * mm});
            skLineSegment(sketch, "E351", {"start": v(59.97, -22.71) * mm, "end": v(59.97, -23.4) * mm});
            skLineSegment(sketch, "E352", {"start": v(-16.55, -23.4) * mm, "end": v(-16.55, -24.22) * mm});
            skLineSegment(sketch, "E353", {"start": v(-16.55, -24.22) * mm, "end": v(-16.88, -26.71) * mm});
            skLineSegment(sketch, "E354", {"start": v(-16.88, -26.71) * mm, "end": v(-17.84, -29.8) * mm});
            skLineSegment(sketch, "E355", {"start": v(-17.84, -29.8) * mm, "end": v(-19.36, -32.6) * mm});
            skLineSegment(sketch, "E356", {"start": v(-19.36, -32.6) * mm, "end": v(-21.37, -35.03) * mm});
            skLineSegment(sketch, "E357", {"start": v(-21.37, -35.03) * mm, "end": v(-23.8, -37.04) * mm});
            skLineSegment(sketch, "E358", {"start": v(-23.8, -37.04) * mm, "end": v(-26.6, -38.56) * mm});
            skLineSegment(sketch, "E359", {"start": v(-26.6, -38.56) * mm, "end": v(-29.69, -39.52) * mm});
            skLineSegment(sketch, "E360", {"start": v(-29.69, -39.52) * mm, "end": v(-32.18, -39.85) * mm});
            skLineSegment(sketch, "E361", {"start": v(-32.18, -39.85) * mm, "end": v(-33, -39.85) * mm});
            skLineSegment(sketch, "E362", {"start": v(-33, -39.85) * mm, "end": v(-33.84, -39.85) * mm});
            skLineSegment(sketch, "E363", {"start": v(-33.84, -39.85) * mm, "end": v(-36.32, -39.52) * mm});
            skLineSegment(sketch, "E364", {"start": v(-36.32, -39.52) * mm, "end": v(-39.41, -38.56) * mm});
            skLineSegment(sketch, "E365", {"start": v(-39.41, -38.56) * mm, "end": v(-42.21, -37.04) * mm});
            skLineSegment(sketch, "E366", {"start": v(-42.21, -37.04) * mm, "end": v(-44.65, -35.03) * mm});
            skLineSegment(sketch, "E367", {"start": v(-44.65, -35.03) * mm, "end": v(-46.66, -32.6) * mm});
            skLineSegment(sketch, "E368", {"start": v(-46.66, -32.6) * mm, "end": v(-48.17, -29.8) * mm});
            skLineSegment(sketch, "E369", {"start": v(-48.17, -29.8) * mm, "end": v(-49.13, -26.71) * mm});
            skLineSegment(sketch, "E370", {"start": v(-49.13, -26.71) * mm, "end": v(-49.47, -24.22) * mm});
            skLineSegment(sketch, "E371", {"start": v(-49.47, -24.22) * mm, "end": v(-49.47, -23.4) * mm});
            skLineSegment(sketch, "E372", {"start": v(-49.47, -23.4) * mm, "end": v(-49.47, -22.56) * mm});
            skLineSegment(sketch, "E373", {"start": v(-49.47, -22.56) * mm, "end": v(-49.13, -20.08) * mm});
            skLineSegment(sketch, "E374", {"start": v(-49.13, -20.08) * mm, "end": v(-48.17, -16.99) * mm});
            skLineSegment(sketch, "E375", {"start": v(-48.17, -16.99) * mm, "end": v(-46.66, -14.19) * mm});
            skLineSegment(sketch, "E376", {"start": v(-46.66, -14.19) * mm, "end": v(-44.65, -11.75) * mm});
            skLineSegment(sketch, "E377", {"start": v(-44.65, -11.75) * mm, "end": v(-42.21, -9.74) * mm});
            skLineSegment(sketch, "E378", {"start": v(-42.21, -9.74) * mm, "end": v(-39.41, -8.23) * mm});
            skLineSegment(sketch, "E379", {"start": v(-39.41, -8.23) * mm, "end": v(-36.32, -7.27) * mm});
            skLineSegment(sketch, "E380", {"start": v(-36.32, -7.27) * mm, "end": v(-33.84, -6.93) * mm});
            skLineSegment(sketch, "E381", {"start": v(-33.84, -6.93) * mm, "end": v(-33, -6.93) * mm});
            skLineSegment(sketch, "E382", {"start": v(-33, -6.93) * mm, "end": v(-32.18, -6.93) * mm});
            skLineSegment(sketch, "E383", {"start": v(-32.18, -6.93) * mm, "end": v(-29.69, -7.27) * mm});
            skLineSegment(sketch, "E384", {"start": v(-29.69, -7.27) * mm, "end": v(-26.6, -8.23) * mm});
            skLineSegment(sketch, "E385", {"start": v(-26.6, -8.23) * mm, "end": v(-23.8, -9.74) * mm});
            skLineSegment(sketch, "E386", {"start": v(-23.8, -9.74) * mm, "end": v(-21.37, -11.75) * mm});
            skLineSegment(sketch, "E387", {"start": v(-21.37, -11.75) * mm, "end": v(-19.36, -14.19) * mm});
            skLineSegment(sketch, "E388", {"start": v(-19.36, -14.19) * mm, "end": v(-17.84, -16.99) * mm});
            skLineSegment(sketch, "E389", {"start": v(-17.84, -16.99) * mm, "end": v(-16.88, -20.08) * mm});
            skLineSegment(sketch, "E390", {"start": v(-16.88, -20.08) * mm, "end": v(-16.55, -22.56) * mm});
            skLineSegment(sketch, "E391", {"start": v(-16.55, -22.56) * mm, "end": v(-16.55, -23.4) * mm});
            skLineSegment(sketch, "E392", {"start": v(50.13, -23.4) * mm, "end": v(50.13, -24.22) * mm});
            skLineSegment(sketch, "E393", {"start": v(50.13, -24.22) * mm, "end": v(49.8, -26.71) * mm});
            skLineSegment(sketch, "E394", {"start": v(49.8, -26.71) * mm, "end": v(48.84, -29.8) * mm});
            skLineSegment(sketch, "E395", {"start": v(48.84, -29.8) * mm, "end": v(47.32, -32.6) * mm});
            skLineSegment(sketch, "E396", {"start": v(47.32, -32.6) * mm, "end": v(45.31, -35.03) * mm});
            skLineSegment(sketch, "E397", {"start": v(45.31, -35.03) * mm, "end": v(42.88, -37.04) * mm});
            skLineSegment(sketch, "E398", {"start": v(42.88, -37.04) * mm, "end": v(40.08, -38.56) * mm});
            skLineSegment(sketch, "E399", {"start": v(40.08, -38.56) * mm, "end": v(36.99, -39.52) * mm});
            skLineSegment(sketch, "E400", {"start": v(36.99, -39.52) * mm, "end": v(34.5, -39.85) * mm});
            skLineSegment(sketch, "E401", {"start": v(34.5, -39.85) * mm, "end": v(33.67, -39.85) * mm});
            skLineSegment(sketch, "E402", {"start": v(33.67, -39.85) * mm, "end": v(32.84, -39.85) * mm});
            skLineSegment(sketch, "E403", {"start": v(32.84, -39.85) * mm, "end": v(30.36, -39.52) * mm});
            skLineSegment(sketch, "E404", {"start": v(30.36, -39.52) * mm, "end": v(27.26, -38.56) * mm});
            skLineSegment(sketch, "E405", {"start": v(27.26, -38.56) * mm, "end": v(24.47, -37.04) * mm});
            skLineSegment(sketch, "E406", {"start": v(24.47, -37.04) * mm, "end": v(22.03, -35.03) * mm});
            skLineSegment(sketch, "E407", {"start": v(22.03, -35.03) * mm, "end": v(20.02, -32.6) * mm});
            skLineSegment(sketch, "E408", {"start": v(20.02, -32.6) * mm, "end": v(18.5, -29.8) * mm});
            skLineSegment(sketch, "E409", {"start": v(18.5, -29.8) * mm, "end": v(17.55, -26.71) * mm});
            skLineSegment(sketch, "E410", {"start": v(17.55, -26.71) * mm, "end": v(17.21, -24.22) * mm});
            skLineSegment(sketch, "E411", {"start": v(17.21, -24.22) * mm, "end": v(17.21, -23.4) * mm});
            skLineSegment(sketch, "E412", {"start": v(17.21, -23.4) * mm, "end": v(17.21, -22.56) * mm});
            skLineSegment(sketch, "E413", {"start": v(17.21, -22.56) * mm, "end": v(17.55, -20.08) * mm});
            skLineSegment(sketch, "E414", {"start": v(17.55, -20.08) * mm, "end": v(18.5, -16.99) * mm});
            skLineSegment(sketch, "E415", {"start": v(18.5, -16.99) * mm, "end": v(20.02, -14.19) * mm});
            skLineSegment(sketch, "E416", {"start": v(20.02, -14.19) * mm, "end": v(22.03, -11.75) * mm});
            skLineSegment(sketch, "E417", {"start": v(22.03, -11.75) * mm, "end": v(24.47, -9.74) * mm});
            skLineSegment(sketch, "E418", {"start": v(24.47, -9.74) * mm, "end": v(27.26, -8.23) * mm});
            skLineSegment(sketch, "E419", {"start": v(27.26, -8.23) * mm, "end": v(30.36, -7.27) * mm});
            skLineSegment(sketch, "E420", {"start": v(30.36, -7.27) * mm, "end": v(32.84, -6.93) * mm});
            skLineSegment(sketch, "E421", {"start": v(32.84, -6.93) * mm, "end": v(33.67, -6.93) * mm});
            skLineSegment(sketch, "E422", {"start": v(33.67, -6.93) * mm, "end": v(34.5, -6.93) * mm});
            skLineSegment(sketch, "E423", {"start": v(34.5, -6.93) * mm, "end": v(36.99, -7.27) * mm});
            skLineSegment(sketch, "E424", {"start": v(36.99, -7.27) * mm, "end": v(40.08, -8.23) * mm});
            skLineSegment(sketch, "E425", {"start": v(40.08, -8.23) * mm, "end": v(42.88, -9.74) * mm});
            skLineSegment(sketch, "E426", {"start": v(42.88, -9.74) * mm, "end": v(45.31, -11.75) * mm});
            skLineSegment(sketch, "E427", {"start": v(45.31, -11.75) * mm, "end": v(47.32, -14.19) * mm});
            skLineSegment(sketch, "E428", {"start": v(47.32, -14.19) * mm, "end": v(48.84, -16.99) * mm});
            skLineSegment(sketch, "E429", {"start": v(48.84, -16.99) * mm, "end": v(49.8, -20.08) * mm});
            skLineSegment(sketch, "E430", {"start": v(49.8, -20.08) * mm, "end": v(50.13, -22.56) * mm});
            skLineSegment(sketch, "E431", {"start": v(50.13, -22.56) * mm, "end": v(50.13, -23.4) * mm});
            skSolve(sketch);
        }
        {
            var Q0;
            Q0=makeQuery(id+"F0.imprint","IMPRINT",FACE,{"disambiguationData":[TD([[makeQuery(id+"F0.imprint","IMPRINT",EDGE,{"derivedFrom":sQuery(id+"F0.wireOp",EDGE,"E0")}),1.0]])]});
            var Q1;
            Q1=makeQuery(id+"F0.imprint","IMPRINT",FACE,{"disambiguationData":[TD([[makeQuery(id+"F0.imprint","IMPRINT",EDGE,{"derivedFrom":sQuery(id+"F0.wireOp",EDGE,"E208")}),-1.0]])]});
            var Q2;
            Q2=makeQuery(id+"F0.imprint","IMPRINT",FACE,{"disambiguationData":[TD([[makeQuery(id+"F0.imprint","IMPRINT",EDGE,{"derivedFrom":sQuery(id+"F0.wireOp",EDGE,"E280")}),-1.0]])]});
            extrude(context, id + "F1", {"entities" : qUnion([Q0, Q1, Q2]), "depth" : 50 * mm});
        }
        {
            var Q0;
            Q0=makeQuery(id+"F1.opExtrude","CAP_EDGE",EDGE,{"disambiguationData":[OSD([sQuery(id+"F0.wireOp",EDGE,"E107")])],"isStart":true});
            var Q1;
            Q1=makeQuery(id+"F1.opExtrude","CAP_EDGE",EDGE,{"disambiguationData":[OSD([sQuery(id+"F0.wireOp",EDGE,"E107")])],"isStart":false});
            var Q2;
            Q2=makeQuery(id+"F1.opExtrude","SWEPT_EDGE",EDGE,{"disambiguationData":[OSD([sQuery(id+"F0.wireOp",EDGE,"E50"),sQuery(id+"F0.wireOp",EDGE,"E51")])]});
            var Q3;
            Q3=makeQuery(id+"F1.opExtrude","SWEPT_EDGE",EDGE,{"disambiguationData":[OSD([sQuery(id+"F0.wireOp",EDGE,"E46"),sQuery(id+"F0.wireOp",EDGE,"E47")])]});
            var Q4;
            Q4=makeQuery(id+"F1.opExtrude","SWEPT_EDGE",EDGE,{"disambiguationData":[OSD([sQuery(id+"F0.wireOp",EDGE,"E42"),sQuery(id+"F0.wireOp",EDGE,"E43")])]});
            fillet(context, id + "F2", {"entities" : qUnion([Q0, Q1, Q2, Q3, Q4]), "radius" : 5 * mm, "tangentPropagation" : true, "allowEdgeOverflow" : false});
        }
    });
